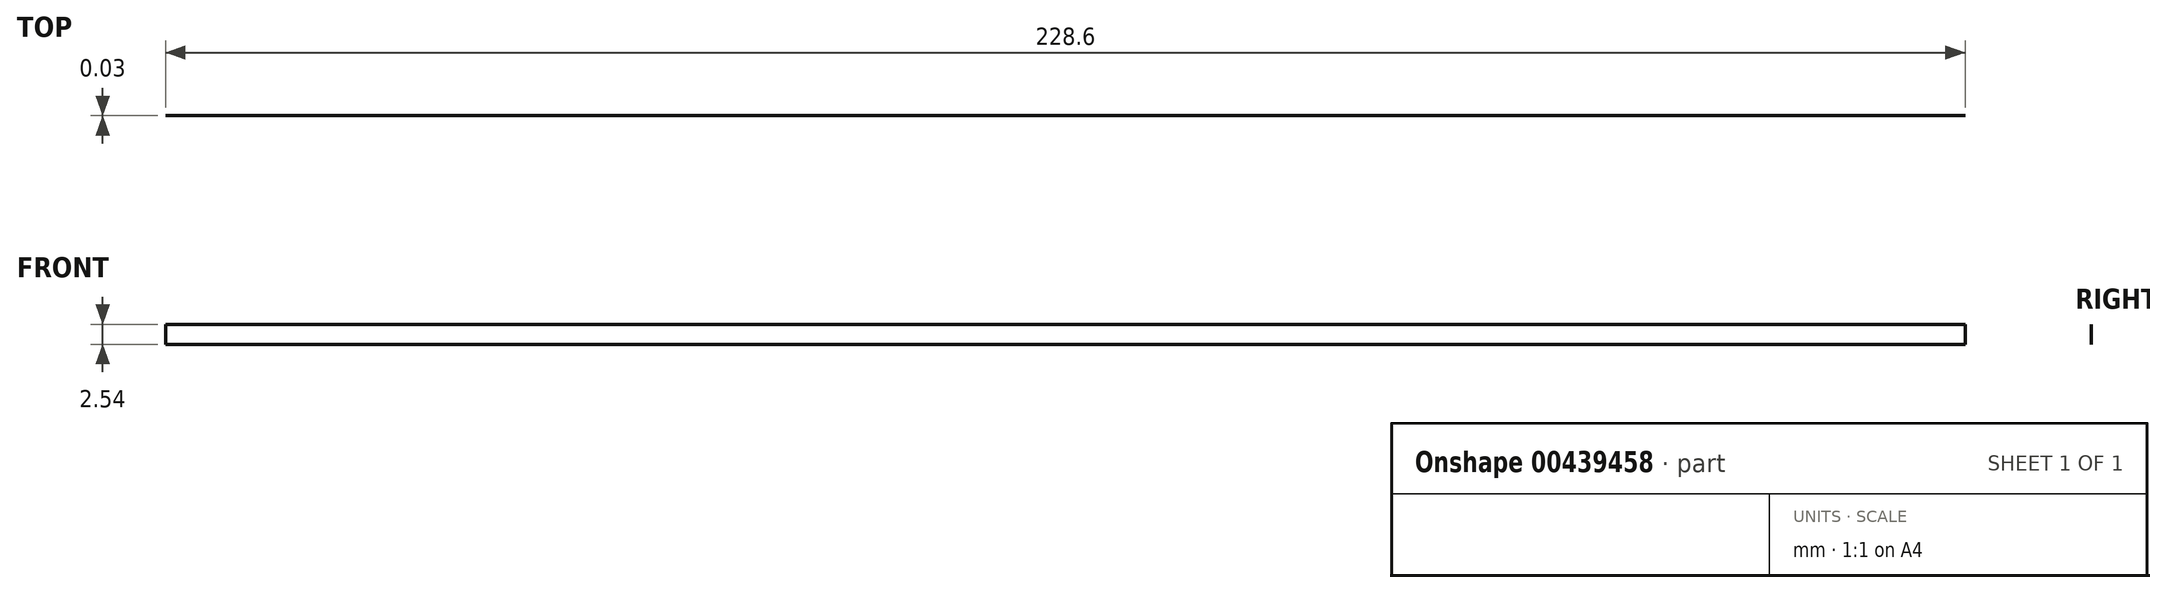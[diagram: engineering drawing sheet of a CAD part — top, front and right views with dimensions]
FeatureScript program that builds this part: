
annotation { "Feature Type Name" : "Feature", "Feature Type Description" : "" }
export const myFeature = defineFeature(function(context is Context, id is Id, definition is map)
    precondition{}
    {
        {
            var Q0;
            Q0=qCreatedBy(makeId("Front.planeOp"),FACE);
            var sketch = newSketch(context, id + "F0", { "sketchPlane" : qUnion([Q0])});
            skLineSegment(sketch, "E0.bottom", {"start": v(-69.43, 0) * mm, "end": v(159.17, 0) * mm});
            skLineSegment(sketch, "E0.top", {"start": v(-69.43, 2.54) * mm, "end": v(159.17, 2.54) * mm});
            skLineSegment(sketch, "E0.left", {"start": v(-69.43, 0) * mm, "end": v(-69.43, 2.54) * mm});
            skLineSegment(sketch, "E0.right", {"start": v(159.17, 0) * mm, "end": v(159.17, 2.54) * mm});
            skSolve(sketch);
        }
        {
            var Q0;
            Q0=makeQuery(id+"F0.imprint","IMPRINT",FACE,{"disambiguationData":[TD([[makeQuery(id+"F0.imprint","IMPRINT",EDGE,{"derivedFrom":sQuery(id+"F0.wireOp",EDGE,"E0.bottom")}),1.0]])]});
            extrude(context, id + "F1", {"entities" : qUnion([Q0]), "depth" : 0.03 * mm});
        }
    });
